# Revit family: EKF_EE_КомплектДляБоковойСтыковкиУниверсальныйFORT_IP31-54_PROxima
name_source: partatom
category: Электрооборудование
units: mm (PartAtom-declared; Revit-internal decimal feet)

## family parameters
Всегда вертикально = Нет
На основе рабочей плоскости = Да
Общий = Да
При загрузке вырезать с полостями = Нет
Размер круглого соединителя = Использовать диаметр
Тип детали = Силовой щит
Точка расчета площади = Нет

## types (2) — shared parameters
ADSK_Единица измерения = шт.
ADSK_Завод-изготовитель = EKF
ADSK_Код изделия = FKBSU
ADSK_Количество = 1
ADSK_Марка = Комплект для боковой стыковки FORT
ADSK_Материал = RAL 7035_Сталь
ADSK_Наименование = Комплект для боковой стыковки FORT универсальный IP31/IP54 EKF PROxima
ADSK_Обозначение = Комплект для боковой стыковки FORT
ADSK_Размер_Высота = 75 мм
ADSK_Размер_Глубина = 65 мм
ADSK_Размер_Ширина = 65 мм
Глубина = 75 мм
Изготовитель = EKF
Серия номенклатуры = PROxima
Степень защиты IP = IP31/IP54
ТВ = EKF_2
Тип = 317 мм
Тип установки = -
Ширина = 65 мм
zero-valued in all types: ADSK_Масса, Отметка по умолчанию

## per-type parameters (varying)
| type | Запчасть |
| Уголок | Вл_Уголок |
| Пластина | Вл_Пластина |
